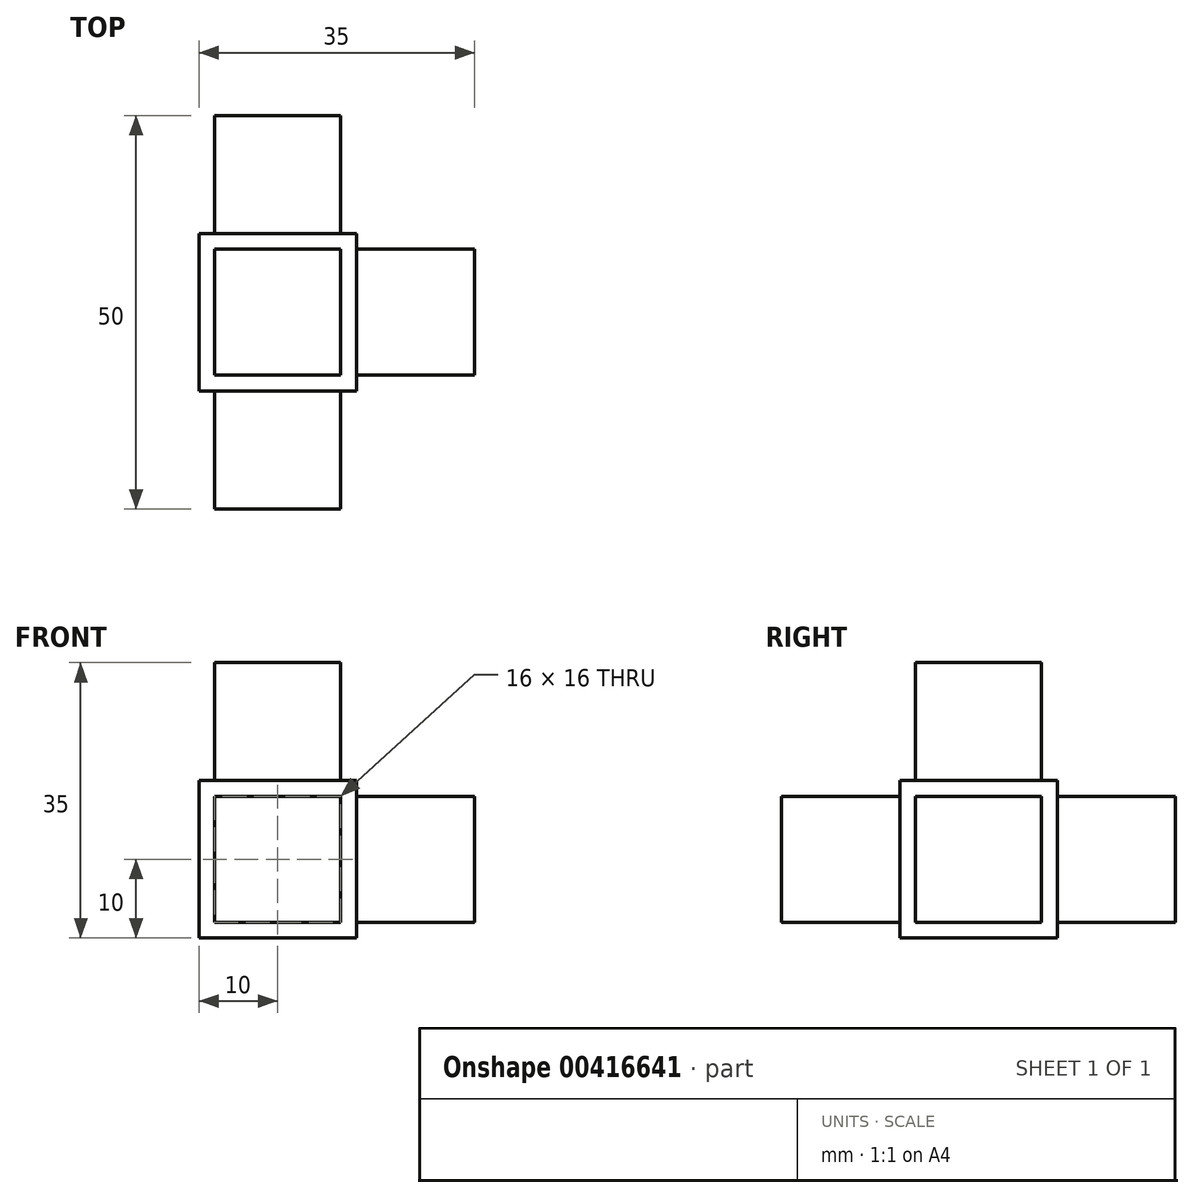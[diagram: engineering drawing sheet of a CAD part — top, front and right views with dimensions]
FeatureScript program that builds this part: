
annotation { "Feature Type Name" : "Feature", "Feature Type Description" : "" }
export const myFeature = defineFeature(function(context is Context, id is Id, definition is map)
    precondition{}
    {
        {
            var Q0;
            Q0=qCreatedBy(makeId("Front.planeOp"),FACE);
            var sketch = newSketch(context, id + "F0", { "sketchPlane" : qUnion([Q0])});
            skLineSegment(sketch, "E0.bottom", {"start": v(0, 0) * mm, "end": v(20, 0) * mm});
            skLineSegment(sketch, "E0.top", {"start": v(0, -20) * mm, "end": v(20, -20) * mm});
            skLineSegment(sketch, "E0.left", {"start": v(0, 0) * mm, "end": v(0, -20) * mm});
            skLineSegment(sketch, "E0.right", {"start": v(20, 0) * mm, "end": v(20, -20) * mm});
            skSolve(sketch);
        }
        {
            var Q0;
            Q0 = qSketchRegion(id + "F0", true);
            extrude(context, id + "F1", {"entities" : qUnion([Q0]), "depth" : 20 * mm});
        }
        {
            var Q0;
            Q0=makeQuery(id+"F1.opExtrude","CAP_FACE",FACE,{"disambiguationData":[OSD([sQuery(id+"F0.wireOp",EDGE,"E0.bottom"),sQuery(id+"F0.wireOp",EDGE,"E0.top"),sQuery(id+"F0.wireOp",EDGE,"E0.left"),sQuery(id+"F0.wireOp",EDGE,"E0.right")])],"isStart":false});
            var sketch = newSketch(context, id + "F2", { "sketchPlane" : qUnion([Q0])});
            skLineSegment(sketch, "E1.bottom", {"start": v(18, -2) * mm, "end": v(2, -2) * mm});
            skLineSegment(sketch, "E1.top", {"start": v(18, -18) * mm, "end": v(2, -18) * mm});
            skLineSegment(sketch, "E1.left", {"start": v(18, -2) * mm, "end": v(18, -18) * mm});
            skLineSegment(sketch, "E1.right", {"start": v(2, -2) * mm, "end": v(2, -18) * mm});
            skSolve(sketch);
        }
        {
            var Q0;
            Q0 = qSketchRegion(id + "F2", true);
            extrude(context, id + "F3", {"entities" : qUnion([Q0]), "operationType" : NewBodyOperationType.ADD, "depth" : 15 * mm});
        }
        {
            var Q0;
            Q0=makeQuery(id+"F1.opExtrude","SWEPT_FACE",FACE,{"disambiguationData":[OSD([sQuery(id+"F0.wireOp",EDGE,"E0.right")])]});
            var sketch = newSketch(context, id + "F4", { "sketchPlane" : qUnion([Q0])});
            skLineSegment(sketch, "E2.bottom", {"start": v(-2, -2) * mm, "end": v(-18, -2) * mm});
            skLineSegment(sketch, "E2.top", {"start": v(-2, -18) * mm, "end": v(-18, -18) * mm});
            skLineSegment(sketch, "E2.left", {"start": v(-2, -2) * mm, "end": v(-2, -18) * mm});
            skLineSegment(sketch, "E2.right", {"start": v(-18, -2) * mm, "end": v(-18, -18) * mm});
            skSolve(sketch);
        }
        {
            var Q0;
            Q0 = qSketchRegion(id + "F4", true);
            extrude(context, id + "F5", {"entities" : qUnion([Q0]), "operationType" : NewBodyOperationType.ADD, "depth" : 15 * mm});
        }
        {
            var Q0;
            Q0=makeQuery(id+"F1.opExtrude","CAP_FACE",FACE,{"disambiguationData":[OSD([sQuery(id+"F0.wireOp",EDGE,"E0.bottom"),sQuery(id+"F0.wireOp",EDGE,"E0.top"),sQuery(id+"F0.wireOp",EDGE,"E0.left"),sQuery(id+"F0.wireOp",EDGE,"E0.right")])],"isStart":true});
            var sketch = newSketch(context, id + "F6", { "sketchPlane" : qUnion([Q0])});
            skLineSegment(sketch, "E3.bottom", {"start": v(-2, -2) * mm, "end": v(-18, -2) * mm});
            skLineSegment(sketch, "E3.top", {"start": v(-2, -18) * mm, "end": v(-18, -18) * mm});
            skLineSegment(sketch, "E3.left", {"start": v(-2, -2) * mm, "end": v(-2, -18) * mm});
            skLineSegment(sketch, "E3.right", {"start": v(-18, -2) * mm, "end": v(-18, -18) * mm});
            skSolve(sketch);
        }
        {
            var Q0;
            Q0 = qSketchRegion(id + "F6", true);
            extrude(context, id + "F7", {"entities" : qUnion([Q0]), "operationType" : NewBodyOperationType.ADD, "depth" : 15 * mm});
        }
        {
            var Q0;
            Q0=makeQuery(id+"F1.opExtrude","SWEPT_FACE",FACE,{"disambiguationData":[OSD([sQuery(id+"F0.wireOp",EDGE,"E0.bottom")])]});
            var sketch = newSketch(context, id + "F8", { "sketchPlane" : qUnion([Q0])});
            skLineSegment(sketch, "E4.bottom", {"start": v(18, -2) * mm, "end": v(2, -2) * mm});
            skLineSegment(sketch, "E4.top", {"start": v(18, -18) * mm, "end": v(2, -18) * mm});
            skLineSegment(sketch, "E4.left", {"start": v(18, -2) * mm, "end": v(18, -18) * mm});
            skLineSegment(sketch, "E4.right", {"start": v(2, -2) * mm, "end": v(2, -18) * mm});
            skSolve(sketch);
        }
        {
            var Q0;
            Q0=makeQuery(id+"F8.imprint","IMPRINT",FACE,{"disambiguationData":[TD([[makeQuery(id+"F8.imprint","IMPRINT",EDGE,{"derivedFrom":sQuery(id+"F8.wireOp",EDGE,"E4.bottom")}),1.0]])]});
            extrude(context, id + "F9", {"entities" : qUnion([Q0]), "operationType" : NewBodyOperationType.ADD, "depth" : 15 * mm});
        }
    });
